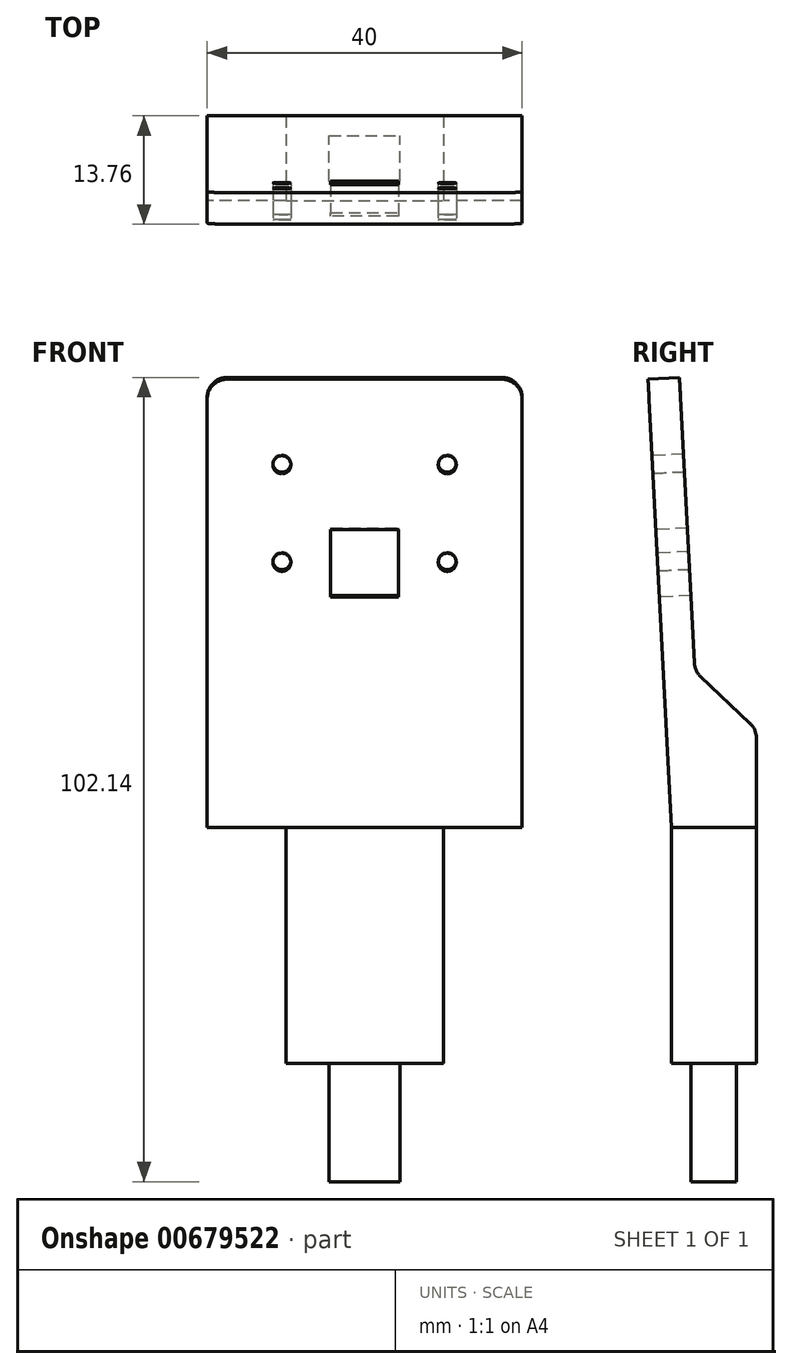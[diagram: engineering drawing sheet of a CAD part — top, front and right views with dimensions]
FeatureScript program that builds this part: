
annotation { "Feature Type Name" : "Feature", "Feature Type Description" : "" }
export const myFeature = defineFeature(function(context is Context, id is Id, definition is map)
    precondition{}
    {
        {
            var Q0;
            Q0=qCreatedBy(makeId("Top.planeOp"),FACE);
            var sketch = newSketch(context, id + "F0", { "sketchPlane" : qUnion([Q0])});
            skLineSegment(sketch, "E0.bottom", {"start": v(-5.52, 4.57) * mm, "end": v(14.48, 4.57) * mm});
            skLineSegment(sketch, "E0.top", {"start": v(-5.52, -6.2) * mm, "end": v(14.48, -6.2) * mm});
            skLineSegment(sketch, "E0.left", {"start": v(-5.52, 4.57) * mm, "end": v(-5.52, -6.2) * mm});
            skLineSegment(sketch, "E0.right", {"start": v(14.48, 4.57) * mm, "end": v(14.48, -6.2) * mm});
            skSolve(sketch);
        }
        {
            var Q0;
            Q0=makeQuery(id+"F0.imprint","IMPRINT",FACE,{"disambiguationData":[TD([[makeQuery(id+"F0.imprint","IMPRINT",EDGE,{"derivedFrom":sQuery(id+"F0.wireOp",EDGE,"E0.bottom")}),-1.0]])]});
            extrude(context, id + "F1", {"entities" : qUnion([Q0]), "depth" : 10 * mm, "offsetDistance" : 25 * mm, "hasSecondDirection" : true, "secondDirectionOppositeDirection" : true, "secondDirectionDepth" : 20 * mm});
        }
        {
            var Q0;
            Q0=makeQuery(id+"F1.opExtrude","SWEPT_FACE",FACE,{"disambiguationData":[OSD([sQuery(id+"F0.wireOp",EDGE,"E0.left")])]});
            var sketch = newSketch(context, id + "F2", { "sketchPlane" : qUnion([Q0])});
            skLineSegment(sketch, "E1", {"start": v(8.66, 56.95) * mm, "end": v(6.2, 10) * mm});
            skLineSegment(sketch, "E2", {"start": v(7.9, 42.47) * mm, "end": v(7.41, 33.12) * mm});
            skLineSegment(sketch, "E3", {"start": v(7.9, 42.47) * mm, "end": v(8.66, 56.95) * mm});
            skLineSegment(sketch, "E4", {"start": v(8.66, 56.95) * mm, "end": v(4.67, 57.16) * mm});
            skPoint(sketch, "E5.trimOffspring.end.orphan", {"position": v(0, 80) * mm});
            skLineSegment(sketch, "E6", {"start": v(4.67, 57.16) * mm, "end": v(3.24, 29.87) * mm});
            skLineSegment(sketch, "E7", {"start": v(-4.57, 10) * mm, "end": v(-4.57, 22.47) * mm});
            skPoint(sketch, "E8.orphan", {"position": v(2.2, 10.1) * mm});
            skPoint(sketch, "E9.start.orphan", {"position": v(9.88, 10.1) * mm});
            skLineSegment(sketch, "E10", {"start": v(3.24, 29.87) * mm, "end": v(-4.57, 22.47) * mm});
            skPoint(sketch, "E11.orphan", {"position": v(-4.57, 29.69) * mm});
            skSolve(sketch);
        }
        {
            var Q0;
            Q0=makeQuery(id+"F2.imprint","IMPRINT",FACE,{"disambiguationData":[TD([[makeQuery(id+"F2.imprint","IMPRINT",EDGE,{"derivedFrom":sQuery(id+"F2.wireOp",EDGE,"E1")}),-1.0]])]});
            extrude(context, id + "F3", {"entities" : qUnion([Q0]), "operationType" : NewBodyOperationType.ADD, "oppositeDirection" : true, "depth" : 30 * mm, "offsetDistance" : 25 * mm, "hasSecondDirection" : true, "secondDirectionOppositeDirection" : false, "secondDirectionDepth" : 10 * mm});
        }
        {
            var Q0;
            Q0=makeQuery(id+"F3.opExtrude","SWEPT_FACE",FACE,{"disambiguationData":[OSD([sQuery(id+"F2.wireOp",EDGE,"E4")])]});
            extrude(context, id + "F4", {"entities" : qUnion([Q0]), "operationType" : NewBodyOperationType.ADD, "depth" : 10 * mm, "offsetDistance" : 25 * mm});
        }
        {
            var Q0;
            {var subQ0=sQuery(id+"F2.wireOp",EDGE,"E3");Q0=makeQuery(id+"F4.boolean.opBoolean","MERGE",FACE,{"derivedFrom":[makeQuery(id+"F3.opExtrude","SWEPT_FACE",FACE,{"disambiguationData":[OSD([sQuery(id+"F2.wireOp",EDGE,"E1"),sQuery(id+"F2.wireOp",EDGE,"E2"),subQ0])]}),makeQuery(id+"F4.opExtrude","SWEPT_FACE",FACE,{"disambiguationData":[OSD([subQ0,sQuery(id+"F2.wireOp",EDGE,"E4")])]})]});}
            var sketch = newSketch(context, id + "F5", { "sketchPlane" : qUnion([Q0])});
            skLineSegment(sketch, "E12", {"start": v(4.48, 48.2) * mm, "end": v(0.18, 48.2) * mm});
            skLineSegment(sketch, "E13", {"start": v(0.18, 48.2) * mm, "end": v(0.18, 39.6) * mm});
            skLineSegment(sketch, "E14", {"start": v(0.18, 39.6) * mm, "end": v(8.78, 39.6) * mm});
            skLineSegment(sketch, "E15", {"start": v(8.78, 39.6) * mm, "end": v(8.78, 48.2) * mm});
            skLineSegment(sketch, "E16", {"start": v(8.78, 48.2) * mm, "end": v(4.48, 48.2) * mm});
            skCircle(sketch, "E17", {"center": v(14.98, 56.44) * mm, "radius": 1.15 * mm});
            skCircle(sketch, "E18", {"center": v(14.98, 44.04) * mm, "radius": 1.15 * mm});
            skCircle(sketch, "E19.MirrorC", {"center": v(-6.02, 44.04) * mm, "radius": 1.15 * mm});
            skCircle(sketch, "E20.MirrorC", {"center": v(-6.02, 56.44) * mm, "radius": 1.15 * mm});
            skPoint(sketch, "E21.start.orphan", {"position": v(4.48, 67.32) * mm});
            skSolve(sketch);
        }
        {
            var Q0;
            Q0 = qSketchRegion(id + "F5", true);
            extrude(context, id + "F6", {"entities" : qUnion([Q0]), "operationType" : NewBodyOperationType.REMOVE, "oppositeDirection" : true, "depth" : 25 * mm, "offsetDistance" : 25 * mm});
        }
        {
            var Q0;
            Q0=makeQuery(id+"F1.opExtrude","CAP_FACE",FACE,{"disambiguationData":[OSD([sQuery(id+"F0.wireOp",EDGE,"E0.bottom"),sQuery(id+"F0.wireOp",EDGE,"E0.top"),sQuery(id+"F0.wireOp",EDGE,"E0.left"),sQuery(id+"F0.wireOp",EDGE,"E0.right")])],"isStart":true});
            var sketch = newSketch(context, id + "F7", { "sketchPlane" : qUnion([Q0])});
            skLineSegment(sketch, "E22.bottom", {"start": v(-0.02, 3.7) * mm, "end": v(8.98, 3.7) * mm});
            skLineSegment(sketch, "E22.top", {"start": v(-0.02, -2.07) * mm, "end": v(8.98, -2.07) * mm});
            skLineSegment(sketch, "E22.left", {"start": v(-0.02, 3.7) * mm, "end": v(-0.02, -2.07) * mm});
            skLineSegment(sketch, "E22.right", {"start": v(8.98, 3.7) * mm, "end": v(8.98, -2.07) * mm});
            skSolve(sketch);
        }
        {
            var Q0;
            Q0 = qSketchRegion(id + "F7", true);
            extrude(context, id + "F8", {"entities" : qUnion([Q0]), "operationType" : NewBodyOperationType.ADD, "depth" : 15 * mm, "offsetDistance" : 25 * mm});
        }
        {
            var Q0;
            {var subQ0=sQuery(id+"F2.wireOp",EDGE,"E4");Q0=makeQuery(id+"F4.opExtrude","CAP_EDGE",EDGE,{"disambiguationData":[OSD([subQ0]),TDD([makeQuery(id+"F3.opExtrude","CAP_EDGE",EDGE,{"disambiguationData":[OSD([subQ0])],"isStart":true})])],"isStart":false});}
            var Q1;
            {var subQ0=sQuery(id+"F2.wireOp",EDGE,"E4");Q1=makeQuery(id+"F4.opExtrude","CAP_EDGE",EDGE,{"disambiguationData":[OSD([subQ0]),TDD([makeQuery(id+"F3.opExtrude","CAP_EDGE",EDGE,{"disambiguationData":[OSD([subQ0])],"isStart":false})])],"isStart":false});}
            fillet(context, id + "F9", {"entities" : qUnion([Q0, Q1]), "radius" : 2.5 * mm, "tangentPropagation" : true, "allowEdgeOverflow" : false});
        }
        {
            var Q0;
            Q0=makeQuery(id+"F3.opExtrude","SWEPT_EDGE",EDGE,{"disambiguationData":[OSD([sQuery(id+"F2.wireOp",EDGE,"DB1Xe39Y-iHYr-sgrD-1E7V-3VLie7vcAiQF"),sQuery(id+"F2.wireOp",EDGE,"E6")])]});
            var Q1;
            Q1=makeQuery(id+"F3.opExtrude","SWEPT_EDGE",EDGE,{"disambiguationData":[OSD([sQuery(id+"F2.wireOp",EDGE,"E7"),sQuery(id+"F2.wireOp",EDGE,"k7ezadbm-x5dQ-US8p-RarK-FocngYKouxzK")])]});
            fillet(context, id + "F10", {"entities" : qUnion([Q0, Q1]), "radius" : 2.5 * mm, "tangentPropagation" : true, "allowEdgeOverflow" : false});
        }
    });
